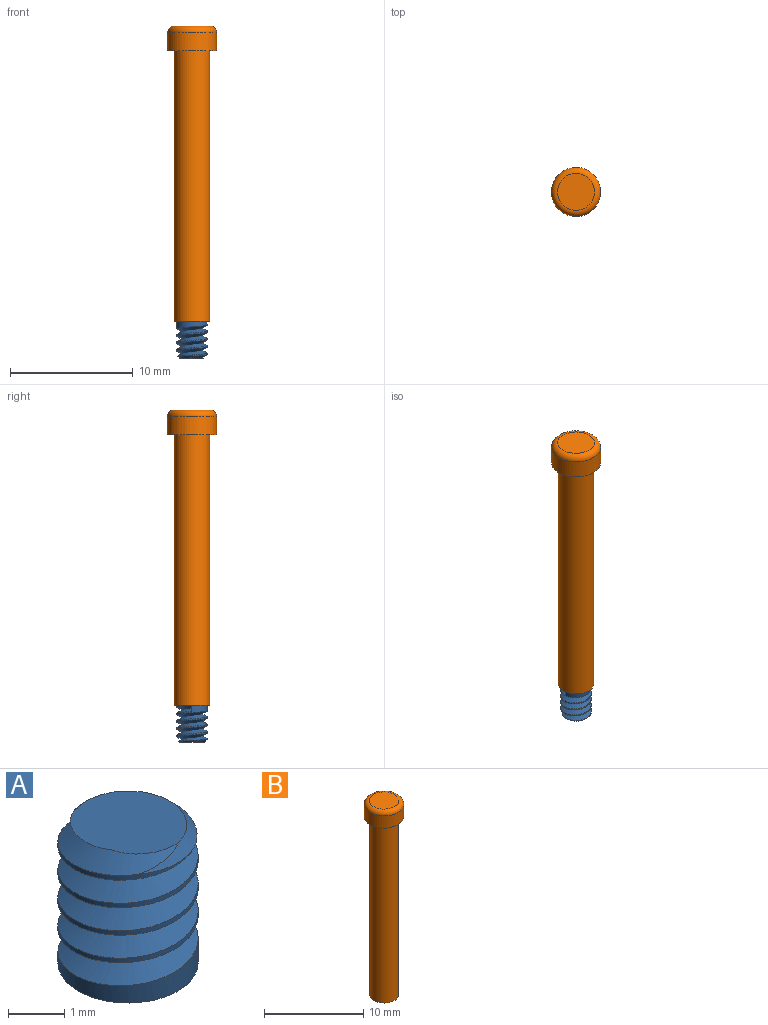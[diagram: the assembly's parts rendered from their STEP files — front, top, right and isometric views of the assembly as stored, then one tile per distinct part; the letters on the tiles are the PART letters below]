
ASSEMBLY  parts=2 mates=1
PART A: 7 faces, bbox 2.6x3x3.3 mm
  f0: cylinder r=1.25mm len=2.8mm, axis (0,0,-1), area 5.9mm2, adj f2,f3,f4,f5,f6
  f1: plane 2.17x2.05mm, normal (0,0,1), area 3.1mm2, adj f3,f5,f6
  f2: plane 2.5x2.5mm, normal (0,0,-1), area 4.9mm2, adj f0
  f3: cone r=1.05mm half-angle=45deg, axis (0,0,-1), area 0.7mm2, adj f0,f1,f5,f6
  f4: plane 0.51x0.44mm, normal (0,1,0), area 0.1mm2, adj f0,f5,f6
  f5: bspline ~3.15x2.89mm, area 15.4mm2, adj f0,f1,f3,f4,f6
  f6: bspline ~2.99x2.5mm, area 13.9mm2, adj f0,f1,f3,f4,f5
PART B: 6 faces, bbox 4.3x4.3x24 mm
  f0: cylinder r=1.45mm len=22mm, axis (0,0,-1), area 200.4mm2, adj f1,f4
  f1: plane 2.9x2.9mm, normal (0,0,-1), area 6.6mm2, adj f0
  f2: cylinder r=2mm len=4mm, axis (0,0,-1), area 18.8mm2, adj f4,f5
  f3: plane 3x3mm, normal (0,0,1), area 7.1mm2, adj f5
  f4: plane 4x4mm, normal (0,0,-1), area 6mm2, adj f0,f2
  f5: torus R=1.5mm, axis (0,0,1), area 9mm2, adj f2,f3
PLACE A rot(axis=(0,-1,0),180deg) t=(-39.78,-4.41,12.58)mm
PLACE B t=(-19.49,-10.77,12.58)mm
MATE parallel B.f0 <-> A.f0  axis (0,0,-1) through (-39.78,-4.41,12.58)mm
